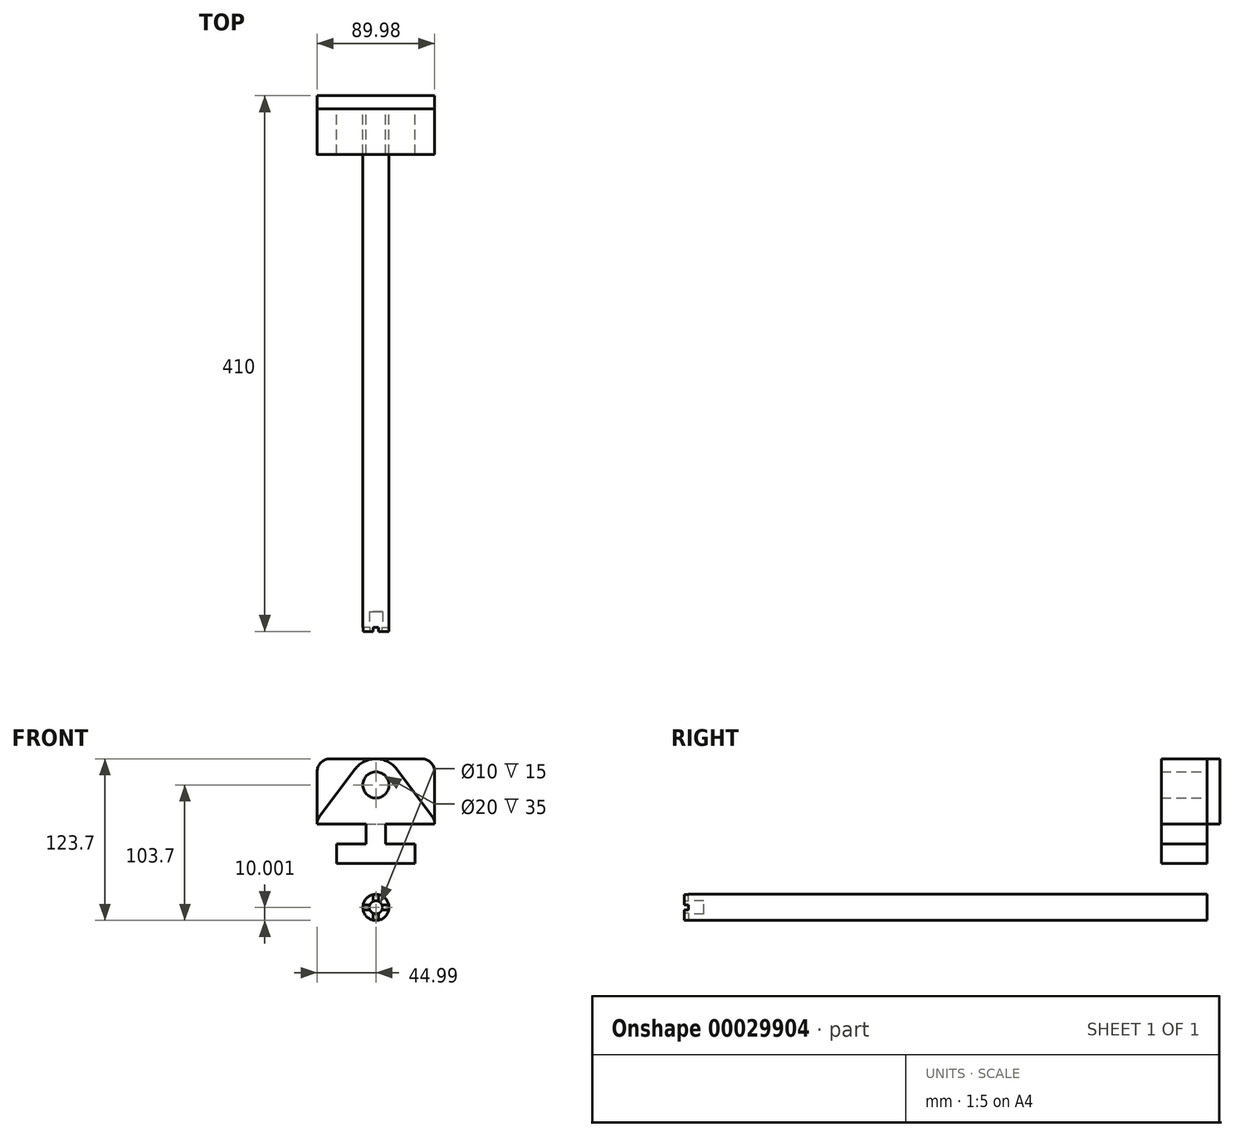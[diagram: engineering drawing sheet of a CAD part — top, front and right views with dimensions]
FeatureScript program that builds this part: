
annotation { "Feature Type Name" : "Feature", "Feature Type Description" : "" }
export const myFeature = defineFeature(function(context is Context, id is Id, definition is map)
    precondition{}
    {
        {
            var Q0;
            Q0=qCreatedBy(makeId("Front.planeOp"),FACE);
            var sketch = newSketch(context, id + "F0", { "sketchPlane" : qUnion([Q0])});
            skLineSegment(sketch, "E0", {"start": v(0, 0) * mm, "end": v(-30, 0) * mm});
            skLineSegment(sketch, "E1", {"start": v(0, 0) * mm, "end": v(30, 0) * mm});
            skLineSegment(sketch, "E2", {"start": v(-30, 0) * mm, "end": v(-30, 15) * mm});
            skLineSegment(sketch, "E3", {"start": v(-30, 15) * mm, "end": v(-7.5, 15) * mm});
            skLineSegment(sketch, "E4", {"start": v(30, 15) * mm, "end": v(30, 0) * mm});
            skLineSegment(sketch, "E5", {"start": v(0, 0) * mm, "end": v(7.5, 0) * mm});
            skLineSegment(sketch, "E6", {"start": v(-7.5, 15) * mm, "end": v(-7.5, 30) * mm});
            skLineSegment(sketch, "E7", {"start": v(7.5, 15) * mm, "end": v(7.5, 30) * mm});
            skLineSegment(sketch, "E8", {"start": v(-7.5, 30) * mm, "end": v(-45, 30) * mm});
            skLineSegment(sketch, "E9", {"start": v(-45, 30) * mm, "end": v(-35, 30) * mm});
            skLineSegment(sketch, "E10", {"start": v(7.5, 30) * mm, "end": v(45, 30) * mm});
            skLineSegment(sketch, "E11.MirrorCS", {"start": v(45, 30) * mm, "end": v(35, 30) * mm});
            skArc(sketch, "E12", {"start": v(-43, 36) * mm, "mid": v(-44.48, 33.16) * mm, "end": v(-45, 30) * mm});
            skArc(sketch, "E13", {"start": v(45, 30) * mm, "mid": v(44.48, 33.16) * mm, "end": v(43, 36) * mm});
            skCircle(sketch, "E14", {"center": v(0, 60) * mm, "radius": 10 * mm});
            skArc(sketch, "E15", {"start": v(16, 72) * mm, "mid": v(0, 80) * mm, "end": v(-16, 72) * mm});
            skLineSegment(sketch, "E16", {"start": v(-43, 36) * mm, "end": v(-16, 72) * mm});
            skLineSegment(sketch, "E17", {"start": v(43, 36) * mm, "end": v(16, 72) * mm});
            skLineSegment(sketch, "E18.trimOffspring", {"start": v(7.5, 15) * mm, "end": v(30, 15) * mm});
            skPoint(sketch, "E19.orphan", {"position": v(0, 30) * mm});
            skPoint(sketch, "E20.start.orphan", {"position": v(0, 80) * mm});
            skPoint(sketch, "E21.MirrorCS.start.orphan", {"position": v(-7.5, 0) * mm});
            skSolve(sketch);
        }
        {
            var Q0;
            Q0=makeQuery(id+"F0.imprint","IMPRINT",FACE,{"disambiguationData":[TD([[makeQuery(id+"F0.imprint","IMPRINT",EDGE,{"derivedFrom":sQuery(id+"F0.wireOp",EDGE,"E0")}),-1.0]])]});
            extrude(context, id + "F1", {"entities" : qUnion([Q0]), "depth" : 35 * mm});
        }
        {
            var Q0;
            Q0=makeQuery(id+"F1.opExtrude","CAP_FACE",FACE,{"disambiguationData":[OSD([sQuery(id+"F0.wireOp",EDGE,"E0"),sQuery(id+"F0.wireOp",EDGE,"E1"),sQuery(id+"F0.wireOp",EDGE,"E2"),sQuery(id+"F0.wireOp",EDGE,"E3"),sQuery(id+"F0.wireOp",EDGE,"E4"),sQuery(id+"F0.wireOp",EDGE,"E5"),sQuery(id+"F0.wireOp",EDGE,"E6"),sQuery(id+"F0.wireOp",EDGE,"E7"),sQuery(id+"F0.wireOp",EDGE,"E8"),sQuery(id+"F0.wireOp",EDGE,"E9"),sQuery(id+"F0.wireOp",EDGE,"E10"),sQuery(id+"F0.wireOp",EDGE,"E11.MirrorCS"),sQuery(id+"F0.wireOp",EDGE,"E12"),sQuery(id+"F0.wireOp",EDGE,"E13"),sQuery(id+"F0.wireOp",EDGE,"E14"),sQuery(id+"F0.wireOp",EDGE,"E15"),sQuery(id+"F0.wireOp",EDGE,"E16"),sQuery(id+"F0.wireOp",EDGE,"E17"),sQuery(id+"F0.wireOp",EDGE,"E18.trimOffspring")])],"isStart":true});
            var sketch = newSketch(context, id + "F2", { "sketchPlane" : qUnion([Q0])});
            skLineSegment(sketch, "E22", {"start": v(0, 80) * mm, "end": v(-35, 80) * mm});
            skLineSegment(sketch, "E23", {"start": v(-45, 70) * mm, "end": v(-45, 30) * mm});
            skLineSegment(sketch, "E24", {"start": v(-35, 80) * mm, "end": v(-35, 70) * mm});
            skArc(sketch, "E25", {"start": v(-35, 80) * mm, "mid": v(-42.06, 77.07) * mm, "end": v(-45, 70) * mm});
            skArc(sketch, "E26.MirrorC", {"start": v(35, 80) * mm, "mid": v(42.06, 77.07) * mm, "end": v(45, 70) * mm});
            skLineSegment(sketch, "E27.MirrorCS", {"start": v(45, 70) * mm, "end": v(45, 30) * mm});
            skLineSegment(sketch, "E28.MirrorCS", {"start": v(0, 80) * mm, "end": v(35, 80) * mm});
            skLineSegment(sketch, "E29", {"start": v(-45, 30) * mm, "end": v(45, 30) * mm});
            skPoint(sketch, "E30.orphan", {"position": v(-45, 80) * mm});
            skPoint(sketch, "E31.orphan", {"position": v(45, 80) * mm});
            skSolve(sketch);
        }
        {
            var Q0;
            Q0 = qSketchRegion(id + "F2", true);
            extrude(context, id + "F3", {"entities" : qUnion([Q0]), "operationType" : NewBodyOperationType.ADD, "depth" : 10 * mm});
        }
        {
            var Q0;
            Q0=qCreatedBy(makeId("Front.planeOp"),FACE);
            var sketch = newSketch(context, id + "F4", { "sketchPlane" : qUnion([Q0])});
            skCircle(sketch, "E32", {"center": v(0, -33.7) * mm, "radius": 10 * mm});
            skSolve(sketch);
        }
        {
            var Q0;
            Q0 = qSketchRegion(id + "F4", true);
            extrude(context, id + "F5", {"entities" : qUnion([Q0]), "depth" : 400 * mm});
        }
        {
            var Q0;
            Q0=makeQuery(id+"F5.opExtrude","CAP_FACE",FACE,{"disambiguationData":[OSD([sQuery(id+"F4.wireOp",EDGE,"E32")])],"isStart":false});
            var sketch = newSketch(context, id + "F6", { "sketchPlane" : qUnion([Q0])});
            skLineSegment(sketch, "E33", {"start": v(-4.58, -35.7) * mm, "end": v(-9.8, -35.7) * mm});
            skLineSegment(sketch, "E34", {"start": v(-2, -38.28) * mm, "end": v(-2, -43.5) * mm});
            skCircle(sketch, "E35", {"center": v(0, -33.7) * mm, "radius": 5 * mm});
            skLineSegment(sketch, "E36.trimOffspring", {"start": v(-4.58, -31.7) * mm, "end": v(-9.8, -31.7) * mm});
            skLineSegment(sketch, "E37.trimOffspring", {"start": v(-2, -29.12) * mm, "end": v(-2, -23.9) * mm});
            skLineSegment(sketch, "E38.trimOffspring", {"start": v(2, -29.12) * mm, "end": v(2, -23.9) * mm});
            skLineSegment(sketch, "E39.trimOffspring", {"start": v(4.58, -31.7) * mm, "end": v(9.8, -31.7) * mm});
            skLineSegment(sketch, "E40.trimOffspring", {"start": v(2, -38.28) * mm, "end": v(2, -43.5) * mm});
            skLineSegment(sketch, "E41.trimOffspring", {"start": v(4.58, -35.7) * mm, "end": v(9.8, -35.7) * mm});
            skSolve(sketch);
        }
        {
            var Q0;
            {var subQ2=sQuery(id+"F6.wireOp",EDGE,"E33");Q0=makeQuery(id+"F6.imprint","IMPRINT",FACE,{"disambiguationData":[TD([[makeQuery(id+"F6.imprint","IMPRINT",EDGE,{"derivedFrom":subQ2}),-1.0]])]});}
            var Q1;
            {var subQ2=sQuery(id+"F6.wireOp",EDGE,"E37.trimOffspring");Q1=makeQuery(id+"F6.imprint","IMPRINT",FACE,{"disambiguationData":[TD([[makeQuery(id+"F6.imprint","IMPRINT",EDGE,{"derivedFrom":subQ2}),-1.0]])]});}
            var Q2;
            {var subQ2=sQuery(id+"F6.wireOp",EDGE,"E39.trimOffspring");Q2=makeQuery(id+"F6.imprint","IMPRINT",FACE,{"disambiguationData":[TD([[makeQuery(id+"F6.imprint","IMPRINT",EDGE,{"derivedFrom":subQ2}),-1.0]])]});}
            var Q3;
            {var subQ2=sQuery(id+"F6.wireOp",EDGE,"E34");Q3=makeQuery(id+"F6.imprint","IMPRINT",FACE,{"disambiguationData":[TD([[makeQuery(id+"F6.imprint","IMPRINT",EDGE,{"derivedFrom":subQ2}),1.0]])]});}
            extrude(context, id + "F7", {"entities" : qUnion([Q0, Q1, Q2, Q3]), "operationType" : NewBodyOperationType.REMOVE, "oppositeDirection" : true, "depth" : 3 * mm});
        }
        {
            var Q0;
            {var subQ0=sQuery(id+"F6.wireOp",EDGE,"E35");var subQ8=makeQuery(id+"F6.imprint","INTERSECT",VERTEX,{"derivedFrom":[subQ0,sQuery(id+"F6.wireOp",EDGE,"E38.trimOffspring")]});Q0=makeQuery(id+"F6.imprint","IMPRINT",FACE,{"disambiguationData":[TD([[makeQuery(id+"F6.imprint","IMPRINT",EDGE,{"disambiguationData":[TD([[subQ8,1.0]])],"derivedFrom":subQ0}),1.0]])]});}
            extrude(context, id + "F8", {"entities" : qUnion([Q0]), "operationType" : NewBodyOperationType.REMOVE, "oppositeDirection" : true, "depth" : 15 * mm});
        }
    });
